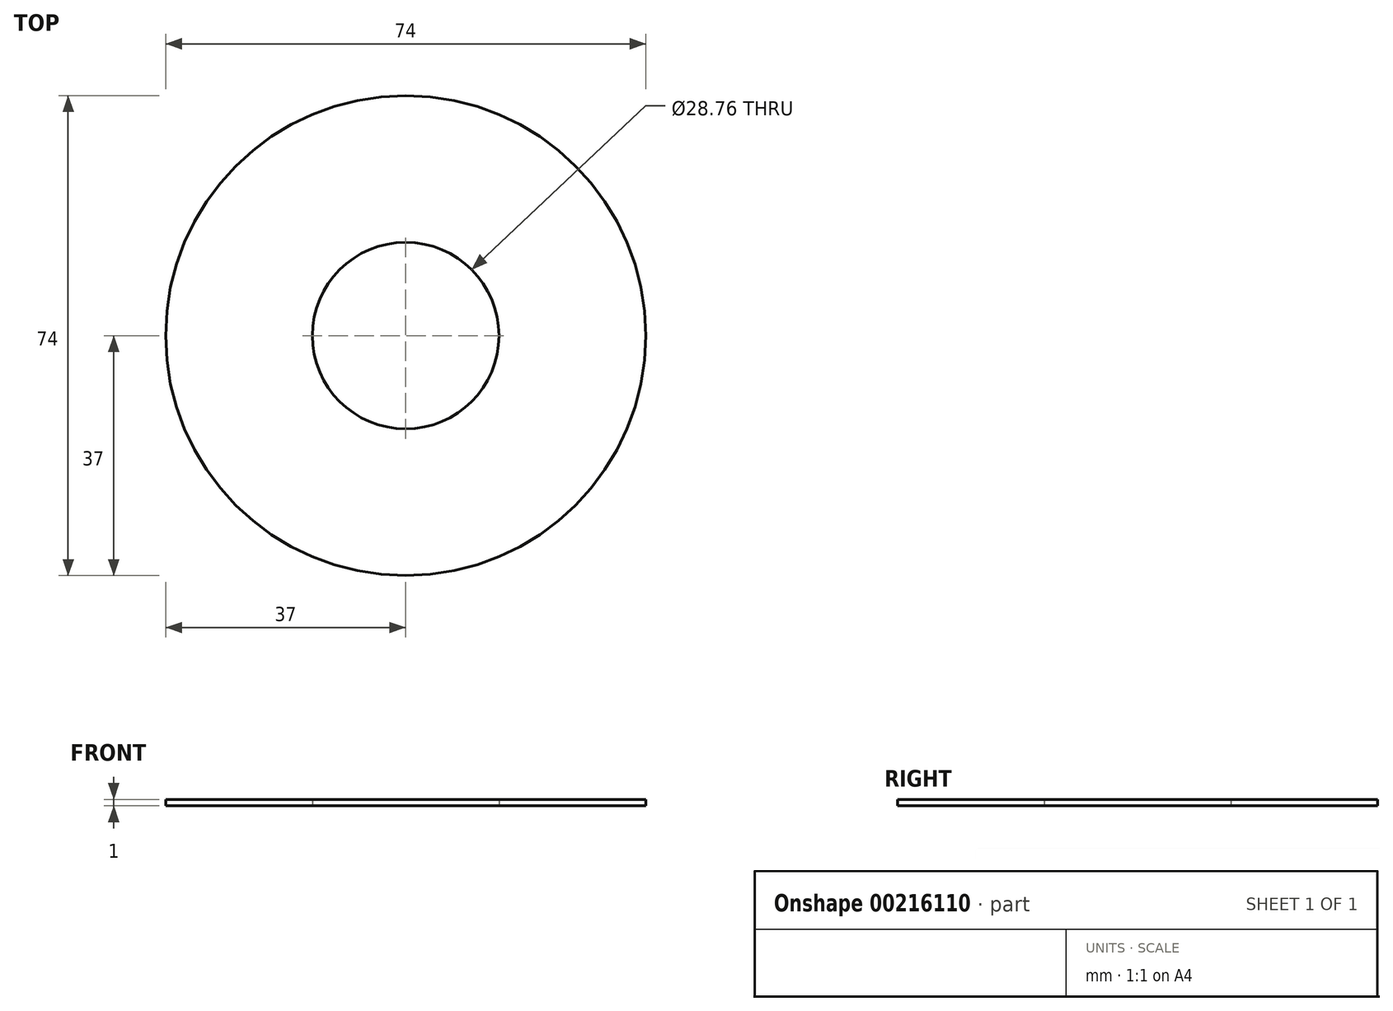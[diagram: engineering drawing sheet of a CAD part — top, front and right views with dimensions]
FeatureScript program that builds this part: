
annotation { "Feature Type Name" : "Feature", "Feature Type Description" : "" }
export const myFeature = defineFeature(function(context is Context, id is Id, definition is map)
    precondition{}
    {
        {
            var Q0;
            Q0=qCreatedBy(makeId("Top.planeOp"),FACE);
            var sketch = newSketch(context, id + "F0", { "sketchPlane" : qUnion([Q0])});
            skCircle(sketch, "E0", {"center": v(0, 0) * mm, "radius": 37 * mm});
            skCircle(sketch, "E1", {"center": v(0, 0) * mm, "radius": 14.38 * mm});
            skSolve(sketch);
        }
        {
            var Q0;
            Q0=makeQuery(id+"F0.imprint","IMPRINT",FACE,{"disambiguationData":[TD([[makeQuery(id+"F0.imprint","IMPRINT",EDGE,{"derivedFrom":sQuery(id+"F0.wireOp",EDGE,"E0")}),1.0]])]});
            extrude(context, id + "F1", {"entities" : qUnion([Q0]), "depth" : 1 * mm});
        }
    });
